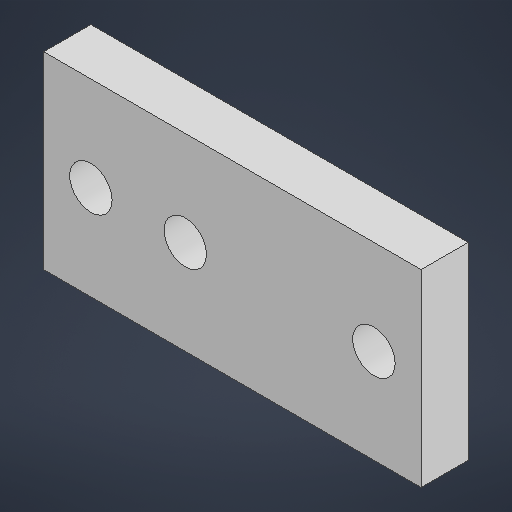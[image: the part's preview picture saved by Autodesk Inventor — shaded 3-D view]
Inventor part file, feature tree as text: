
AUTODESK INVENTOR PART (.ipt)
format: ipt  version: 2025.1 (Build 291241000, 241)  size: 161,792 bytes
history: native  units: mm
features: extrude x1, sketch x1
ambient origin geometry x8: Origin, YZ Plane, XZ Plane, XY Plane, X Axis, Y Axis, Z Axis, Center Point
bodies: Solid1 (feature_tree)
feature tree (2):
  extrude  "Extrusion1"  Depth=10.0mm
  sketch  "Sketch1"  dims[d0=4.5mm d1=10.0mm d2=5.0mm d3=20.0mm d4=4.5mm d5=20.0mm d6=5.0mm d7=5.0mm d8=0.0mm]
